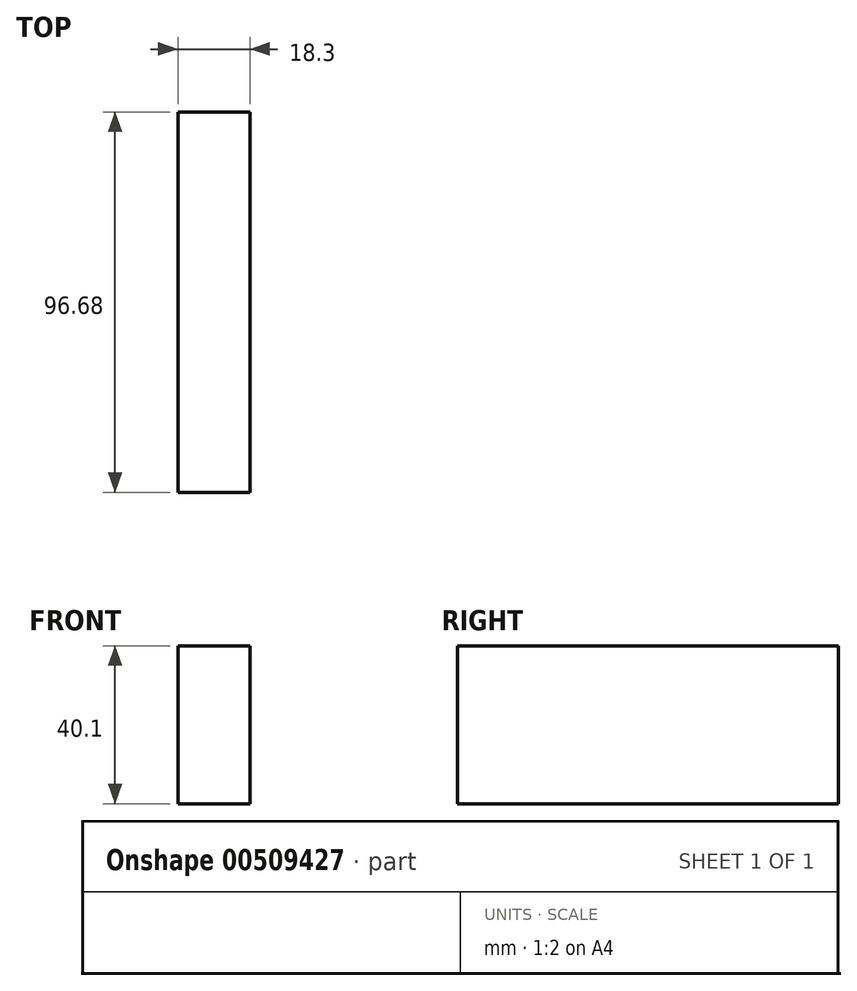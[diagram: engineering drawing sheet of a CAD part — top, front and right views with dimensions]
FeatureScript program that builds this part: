
annotation { "Feature Type Name" : "Feature", "Feature Type Description" : "" }
export const myFeature = defineFeature(function(context is Context, id is Id, definition is map)
    precondition{}
    {
        {
            var Q0;
            Q0=qCreatedBy(makeId("Front.planeOp"),FACE);
            var sketch = newSketch(context, id + "F0", { "sketchPlane" : qUnion([Q0])});
            skLineSegment(sketch, "E0.bottom", {"start": v(59.04, 0) * mm, "end": v(77.34, 0) * mm});
            skLineSegment(sketch, "E0.top", {"start": v(59.04, 40.1) * mm, "end": v(77.34, 40.1) * mm});
            skLineSegment(sketch, "E0.left", {"start": v(59.04, 0) * mm, "end": v(59.04, 40.1) * mm});
            skLineSegment(sketch, "E0.right", {"start": v(77.34, 0) * mm, "end": v(77.34, 40.1) * mm});
            skSolve(sketch);
        }
        {
            var Q0;
            Q0=makeQuery(id+"F0.imprint","IMPRINT",FACE,{"disambiguationData":[TD([[makeQuery(id+"F0.imprint","IMPRINT",EDGE,{"derivedFrom":sQuery(id+"F0.wireOp",EDGE,"E0.bottom")}),1.0]])]});
            extrude(context, id + "F1", {"entities" : qUnion([Q0]), "depth" : 96.68 * mm});
        }
    });
